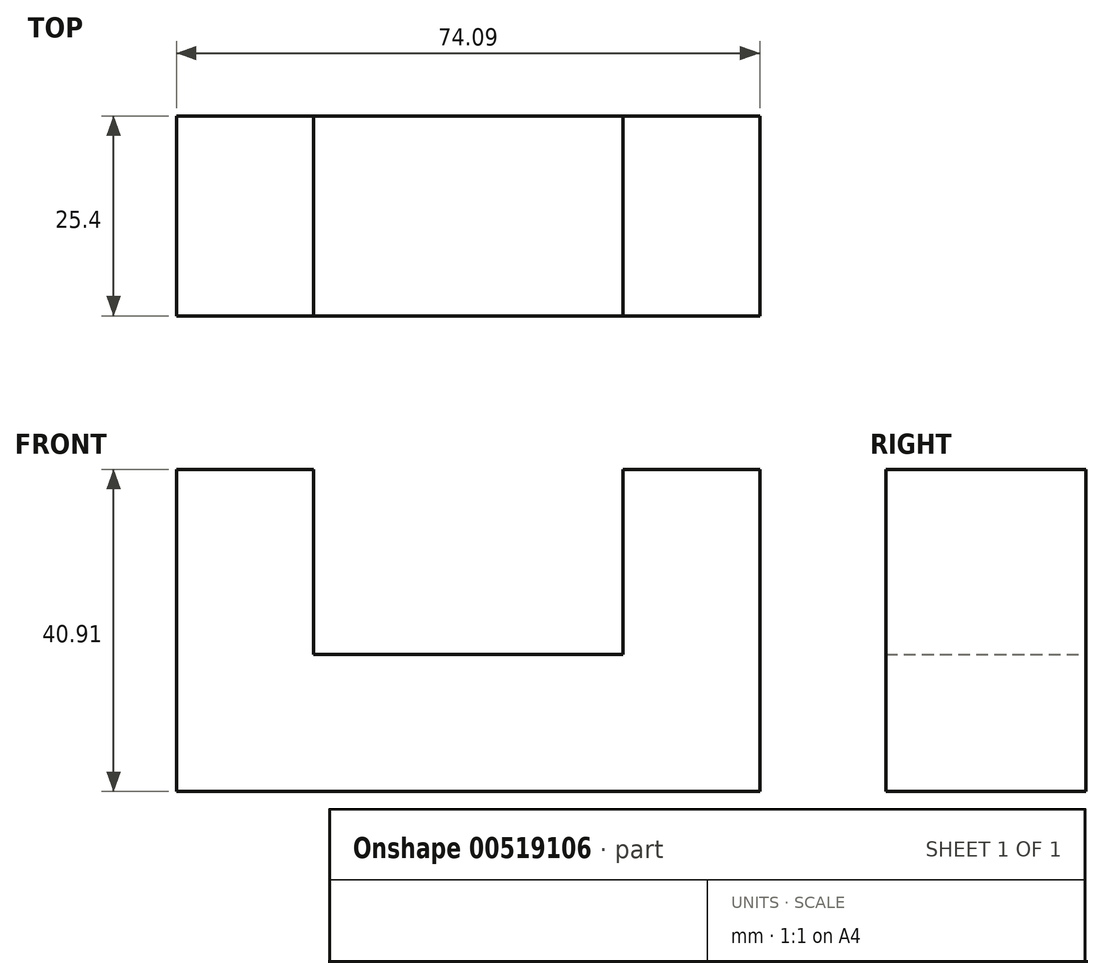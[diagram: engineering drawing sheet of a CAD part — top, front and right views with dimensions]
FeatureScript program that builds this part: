
annotation { "Feature Type Name" : "Feature", "Feature Type Description" : "" }
export const myFeature = defineFeature(function(context is Context, id is Id, definition is map)
    precondition{}
    {
        {
            var Q0;
            Q0=qCreatedBy(makeId("Front.planeOp"),FACE);
            var sketch = newSketch(context, id + "F0", { "sketchPlane" : qUnion([Q0])});
            skLineSegment(sketch, "E0.bottom", {"start": v(0, 0) * mm, "end": v(74.09, 0) * mm});
            skLineSegment(sketch, "E0.top", {"start": v(0, 40.9) * mm, "end": v(17.4, 40.9) * mm});
            skLineSegment(sketch, "E0.left", {"start": v(0, 0) * mm, "end": v(0, 40.9) * mm});
            skLineSegment(sketch, "E0.right", {"start": v(74.09, 0) * mm, "end": v(74.09, 40.9) * mm});
            skLineSegment(sketch, "E1.top", {"start": v(17.4, 17.4) * mm, "end": v(56.69, 17.4) * mm});
            skLineSegment(sketch, "E1.left", {"start": v(17.4, 40.9) * mm, "end": v(17.4, 17.4) * mm});
            skLineSegment(sketch, "E1.right", {"start": v(56.69, 40.9) * mm, "end": v(56.69, 17.4) * mm});
            skLineSegment(sketch, "E2.trimOffspring", {"start": v(56.69, 40.9) * mm, "end": v(74.09, 40.9) * mm});
            skSolve(sketch);
        }
        {
            var Q0;
            Q0=makeQuery(id+"F0.imprint","IMPRINT",FACE,{"disambiguationData":[TD([[makeQuery(id+"F0.imprint","IMPRINT",EDGE,{"derivedFrom":sQuery(id+"F0.wireOp",EDGE,"E0.bottom")}),1.0]])]});
            extrude(context, id + "F1", {"entities" : qUnion([Q0]), "depth" : 25.4 * mm});
        }
    });
